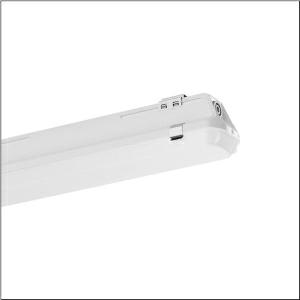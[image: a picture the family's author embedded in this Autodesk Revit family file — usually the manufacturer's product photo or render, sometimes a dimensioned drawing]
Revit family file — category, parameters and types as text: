
# Revit family: monsun_r__11_emergency_51fp207p467h3g_ea6c
name_source: partatom
category: Lighting Fixtures
units: mm (PartAtom-declared; Revit-internal decimal feet)

## family parameters
Cut with Voids When Loaded = No
Host = Face
Light Source = No
Part Type = Normal
Room Calculation Point = No
Round Connector Dimension = Use Diameter
Shared = No

## types (1)
- Monsun® 11 emergency (1 x LED, 5450 lm, 37.2 W, 4000K)
    Apparent Load = 37 VA
    CIE Flux Codes = 45 75 93 94 100
    Color Rendering = 80
    Color Temperature = 4000K
    Default Elevation = 1800 mm
    Description = Monsun® 11 emergency, damp-proof luminaire, chain hanger, primary optical cover: enclosure, of PC, light emission: direct distribution, primary light characteristic: symmetric, installation type: suspended mounting, surface-mounted, horizontal mounting, vertical mounting, LED, rated luminous flux: 5.450lm, luminous efficacy: 147lm/W, light colour: 840, colour temperature: 4000K, control gear: ECG, with terminal, 4-pole, max. 2.5mm², mains connection: 220..240V, AC, 50/60Hz, rated input power: 37W, control gear: single battery element, battery: NiCd, 4,5Ah, mains connection: 230V, luminaire housing, of glass-fibre reinforced polyester, uncoated, bright grey, incl. chain hanger, length: 1.590mm, width: 90mm, height: 88mm, clip for enclosure, of stainless steel (V2A), ceiling mounting element, of stainless steel (V2A), chain hanger, of stainless steel (V2A), protection rating (complete): IP66, insulation class (complete): insulation class I (protective earthing), certification: CE, UKCA, protection symbol: D, impact resistance: IK08, permissible operating ambient temperature: +5..+35°C, standard: EN 50419, EN 60598-2-1, EN 60598-2-22, no direct snow, no direct sun, no direct rain, for indoor or canopied outdoor use, corresponds to IFS (International Featured Standards) requirements for safety and quality in the food industry, contact your sales advisor before using the luminaires in applications with unclear chemical exposure, large temperature fluctuations or condensation-forming humidity, LABS conformity tested according to VDMA 24364:2018-05, packaging unit: 1 piece
    Height = 89 mm
    Lamp = 1 x LED
    Lamp Light Flux = 5450 lm
    Lamp Power = 37.2 W
    Lamp count = 1
    Length = 1590 mm
    Luminous efficacy = 147 lm/W
    Manufacturer = Siteco
    ModVariant = No
    Model = 51FP207P467H3G
    Mounting Place = Ceiling
    Mounting Type = Surface mounted
    Number of Poles = 1
    OnlyDefault = Yes
    Power Factor = 1
    Product Name = Monsun® 11 emergency
    Product group = damp-proof luminaire
    ProductGroupID = 300
    Protection Class = Protection class I
    Protection Degree = IP 66
    RLX_Detail_Level = 1
    RLX_Emergency_Light_Flux = 0 lm
    RLX_Emergency_Type = 0
    RLX_Emergency_Type_DB = No
    RlxData = <blob elided: 89081 chars, md5=6c2a3b4f>
    Socket = socket
    Standby Power = 0 W
    System Light Flux = 5450 lm
    System Power = 37 W
    Type Comments = Product without accessories
    Type Image = l_1319650.jpg
    URL = http://relux.com
    VarID = ---
    Voltage = 0 V
    Weight = 0.00 kg
    Width = 90 mm

## geometry (parser evidence)
native form markers: Blend x4, Sweep x12
no freeform markers — native parametric forms only
